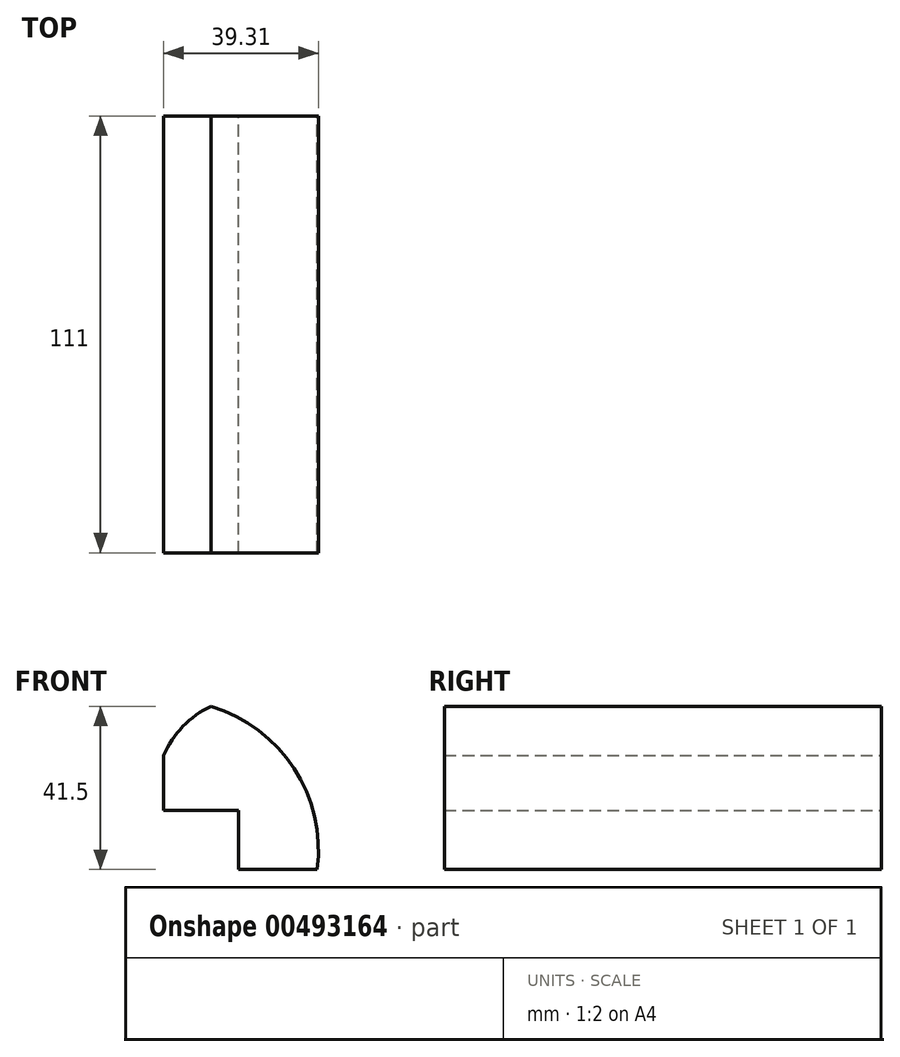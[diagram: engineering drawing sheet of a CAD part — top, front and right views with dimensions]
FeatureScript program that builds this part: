
annotation { "Feature Type Name" : "Feature", "Feature Type Description" : "" }
export const myFeature = defineFeature(function(context is Context, id is Id, definition is map)
    precondition{}
    {
        {
            var Q0;
            Q0=qCreatedBy(makeId("Front.planeOp"),FACE);
            var sketch = newSketch(context, id + "F0", { "sketchPlane" : qUnion([Q0])});
            skLineSegment(sketch, "E0.bottom", {"start": v(0, 0) * mm, "end": v(19, 0) * mm, "construction": true});
            skLineSegment(sketch, "E0.top", {"start": v(0, 15) * mm, "end": v(19, 15) * mm});
            skLineSegment(sketch, "E0.left", {"start": v(0, 0) * mm, "end": v(0, 15) * mm, "construction": true});
            skLineSegment(sketch, "E0.right", {"start": v(19, 0) * mm, "end": v(19, 15) * mm});
            skLineSegment(sketch, "E1", {"start": v(19, 0) * mm, "end": v(39, 0) * mm});
            skLineSegment(sketch, "E2", {"start": v(0, 15) * mm, "end": v(0, 29) * mm});
            skArc(sketch, "E3", {"start": v(12, 41.5) * mm, "mid": v(4.84, 36.36) * mm, "end": v(0, 29) * mm});
            skArc(sketch, "E4", {"start": v(39, 0) * mm, "mid": v(33.13, 25.71) * mm, "end": v(12, 41.5) * mm});
            skLineSegment(sketch, "E5", {"start": v(12, 41.5) * mm, "end": v(12, 15) * mm, "construction": true});
            skSolve(sketch);
        }
        {
            var Q0;
            Q0 = qSketchRegion(id + "F0", true);
            extrude(context, id + "F1", {"entities" : qUnion([Q0]), "depth" : 111 * mm});
        }
    });
